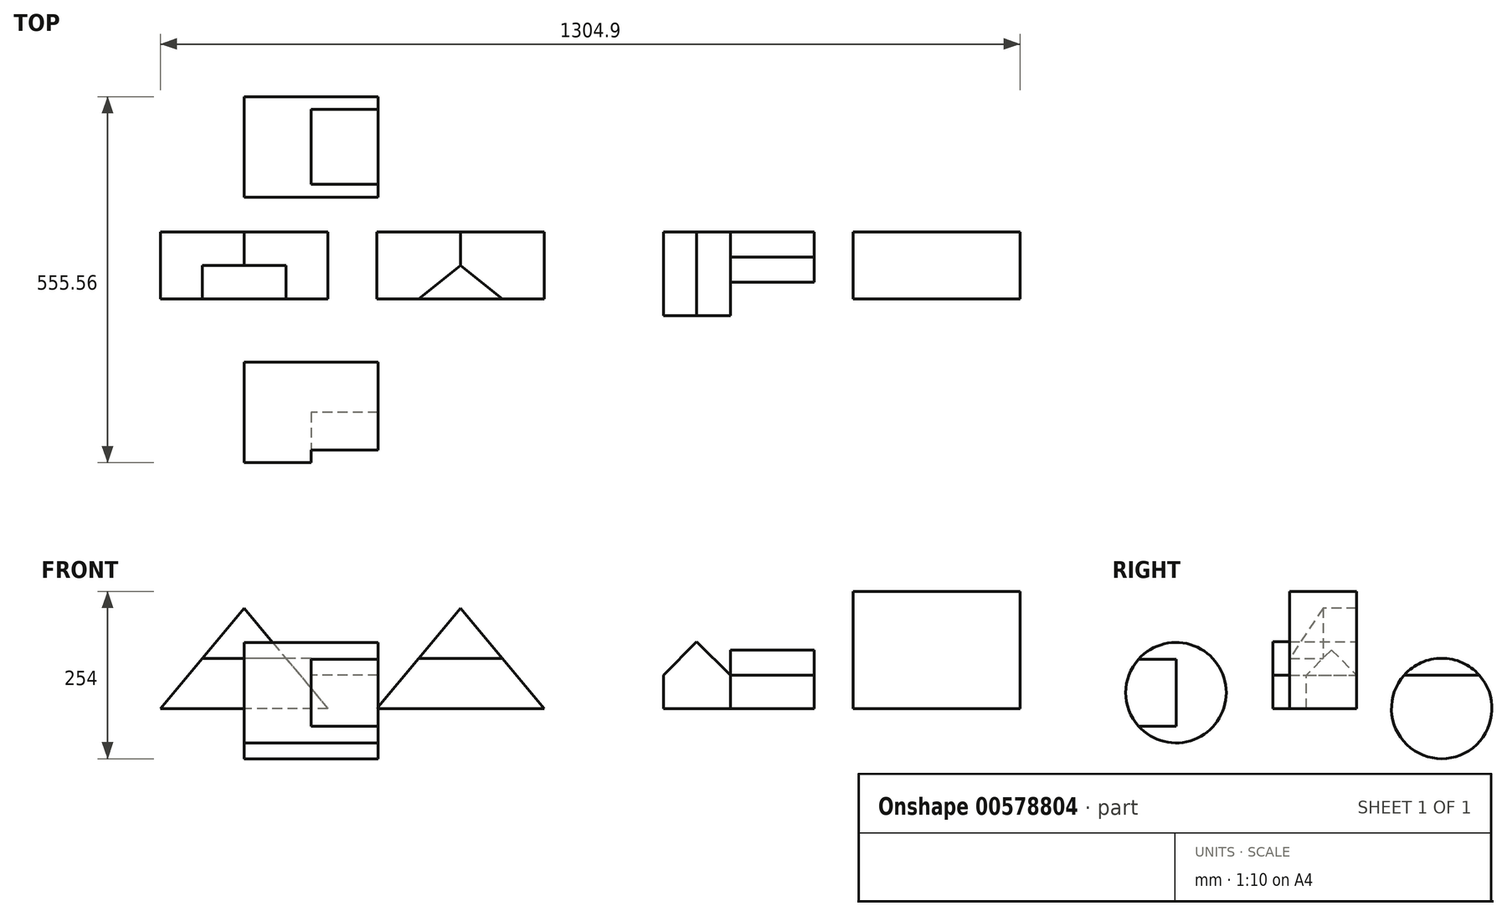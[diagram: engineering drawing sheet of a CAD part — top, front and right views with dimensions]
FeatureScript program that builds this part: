
annotation { "Feature Type Name" : "Feature", "Feature Type Description" : "" }
export const myFeature = defineFeature(function(context is Context, id is Id, definition is map)
    precondition{}
    {
        {
            var Q0;
            Q0=qCreatedBy(makeId("Front.planeOp"),FACE);
            var sketch = newSketch(context, id + "F0", { "sketchPlane" : qUnion([Q0])});
            skLineSegment(sketch, "E0", {"start": v(0, 0) * mm, "end": v(127, 0) * mm});
            skLineSegment(sketch, "E1", {"start": v(0, 0) * mm, "end": v(-127, 0) * mm});
            skLineSegment(sketch, "E2", {"start": v(0, 0) * mm, "end": v(0, 76.2) * mm});
            skLineSegment(sketch, "E3", {"start": v(0, 76.2) * mm, "end": v(0, 152.4) * mm});
            skLineSegment(sketch, "E4", {"start": v(0, 152.4) * mm, "end": v(127, 0) * mm});
            skLineSegment(sketch, "E5", {"start": v(0, 152.4) * mm, "end": v(-127, 0) * mm});
            skLineSegment(sketch, "E6", {"start": v(0, 76.2) * mm, "end": v(63.5, 76.2) * mm});
            skLineSegment(sketch, "E7", {"start": v(63.5, 76.2) * mm, "end": v(-63.5, 76.2) * mm});
            skSolve(sketch);
        }
        {
            var Q0;
            {var subQ0=sQuery(id+"F0.wireOp",EDGE,"E1");Q0=makeQuery(id+"F0.imprint","IMPRINT",FACE,{"disambiguationData":[TD([[makeQuery(id+"F0.imprint","IMPRINT",EDGE,{"derivedFrom":subQ0}),-1.0]])]});}
            var Q1;
            {var subQ0=sQuery(id+"F0.wireOp",EDGE,"E0");Q1=makeQuery(id+"F0.imprint","IMPRINT",FACE,{"disambiguationData":[TD([[makeQuery(id+"F0.imprint","IMPRINT",EDGE,{"derivedFrom":subQ0}),1.0]])]});}
            extrude(context, id + "F1", {"entities" : qUnion([Q0, Q1]), "depth" : 101.6 * mm, "offsetDistance" : 25.4 * mm});
        }
        {
            var Q0;
            Q0 = qSketchRegion(id + "F0", true);
            extrude(context, id + "F2", {"entities" : qUnion([Q0]), "operationType" : NewBodyOperationType.ADD, "depth" : 50.8 * mm, "offsetDistance" : 25.4 * mm});
        }
        {
            var Q0;
            Q0=qCreatedBy(makeId("Front.planeOp"),FACE);
            var sketch = newSketch(context, id + "F3", { "sketchPlane" : qUnion([Q0])});
            skLineSegment(sketch, "E8", {"start": v(201.55, 0) * mm, "end": v(455.55, 0) * mm});
            skLineSegment(sketch, "E9", {"start": v(201.55, 0) * mm, "end": v(201.55, 152.4) * mm});
            skLineSegment(sketch, "E10", {"start": v(201.55, 152.4) * mm, "end": v(455.55, 152.4) * mm});
            skLineSegment(sketch, "E11", {"start": v(455.55, 152.4) * mm, "end": v(455.55, 0) * mm});
            skSolve(sketch);
        }
        {
            var Q0;
            Q0=makeQuery(id+"F3.imprint","IMPRINT",FACE,{"disambiguationData":[TD([[makeQuery(id+"F3.imprint","IMPRINT",EDGE,{"derivedFrom":sQuery(id+"F3.wireOp",EDGE,"E8")}),1.0]])]});
            extrude(context, id + "F4", {"entities" : qUnion([Q0]), "depth" : 101.6 * mm, "offsetDistance" : 25.4 * mm});
        }
        {
            var Q0;
            Q0=makeQuery(id+"F4.opExtrude","SWEPT_FACE",FACE,{"disambiguationData":[OSD([sQuery(id+"F3.wireOp",EDGE,"E11")])]});
            var sketch = newSketch(context, id + "F5", { "sketchPlane" : qUnion([Q0])});
            skLineSegment(sketch, "E12", {"start": v(-50.8, 152.4) * mm, "end": v(-101.6, 76.2) * mm});
            skSolve(sketch);
        }
        {
            var Q0;
            Q0=makeQuery(id+"F4.opExtrude","CAP_FACE",FACE,{"disambiguationData":[OSD([sQuery(id+"F3.wireOp",EDGE,"E8"),sQuery(id+"F3.wireOp",EDGE,"E9"),sQuery(id+"F3.wireOp",EDGE,"E10"),sQuery(id+"F3.wireOp",EDGE,"E11")])],"isStart":false});
            var sketch = newSketch(context, id + "F6", { "sketchPlane" : qUnion([Q0])});
            skLineSegment(sketch, "E13", {"start": v(328.55, 152.4) * mm, "end": v(455.55, 0) * mm});
            skLineSegment(sketch, "E14", {"start": v(455.55, 0) * mm, "end": v(201.55, 0) * mm});
            skLineSegment(sketch, "E15", {"start": v(201.55, 0) * mm, "end": v(328.55, 152.4) * mm});
            skSolve(sketch);
        }
        {
            var Q0;
            {var subQ0=sQuery(id+"F5.wireOp",EDGE,"E12");Q0=makeQuery(id+"F5.imprint","IMPRINT",FACE,{"disambiguationData":[TD([[makeQuery(id+"F5.imprint","IMPRINT",EDGE,{"derivedFrom":subQ0}),-1.0]])]});}
            extrude(context, id + "F7", {"entities" : qUnion([Q0]), "operationType" : NewBodyOperationType.REMOVE, "oppositeDirection" : true, "depth" : 254 * mm, "offsetDistance" : 25.4 * mm});
        }
        {
            var Q0;
            {var subQ0=sQuery(id+"F6.wireOp",EDGE,"E15");Q0=makeQuery(id+"F6.imprint","IMPRINT",FACE,{"disambiguationData":[TD([[makeQuery(id+"F6.imprint","IMPRINT",EDGE,{"derivedFrom":subQ0}),1.0]])]});}
            extrude(context, id + "F8", {"entities" : qUnion([Q0]), "operationType" : NewBodyOperationType.REMOVE, "oppositeDirection" : true, "depth" : 101.6 * mm, "offsetDistance" : 25.4 * mm});
        }
        {
            var Q0;
            {var subQ0=sQuery(id+"F6.wireOp",EDGE,"E13");Q0=makeQuery(id+"F6.imprint","IMPRINT",FACE,{"disambiguationData":[TD([[makeQuery(id+"F6.imprint","IMPRINT",EDGE,{"derivedFrom":subQ0}),1.0]])]});}
            extrude(context, id + "F9", {"entities" : qUnion([Q0]), "operationType" : NewBodyOperationType.REMOVE, "oppositeDirection" : true, "depth" : 101.6 * mm, "offsetDistance" : 25.4 * mm});
        }
        {
            var Q0;
            Q0=qCreatedBy(makeId("Front.planeOp"),FACE);
            var sketch = newSketch(context, id + "F10", { "sketchPlane" : qUnion([Q0])});
            skLineSegment(sketch, "E16", {"start": v(636.4, 0) * mm, "end": v(738, 0) * mm});
            skLineSegment(sketch, "E17", {"start": v(738, 0) * mm, "end": v(738, 50.8) * mm});
            skLineSegment(sketch, "E18", {"start": v(686.75, 101.6) * mm, "end": v(738, 50.8) * mm});
            skLineSegment(sketch, "E19", {"start": v(636.4, 0) * mm, "end": v(636.4, 50.8) * mm});
            skLineSegment(sketch, "E20", {"start": v(636.4, 50.8) * mm, "end": v(686.75, 101.6) * mm});
            skSolve(sketch);
        }
        {
            var Q0;
            Q0=makeQuery(id+"F10.imprint","IMPRINT",FACE,{"disambiguationData":[TD([[makeQuery(id+"F10.imprint","IMPRINT",EDGE,{"derivedFrom":sQuery(id+"F10.wireOp",EDGE,"E16")}),1.0]])]});
            extrude(context, id + "F11", {"entities" : qUnion([Q0]), "depth" : 127 * mm, "offsetDistance" : 25.4 * mm});
        }
        {
            var Q0;
            Q0=makeQuery(id+"F11.opExtrude","SWEPT_FACE",FACE,{"disambiguationData":[OSD([sQuery(id+"F10.wireOp",EDGE,"E17")])]});
            cPlane(context, id + "F12", {"entities" : qUnion([Q0]), "cplaneType" : CPlaneType.OFFSET, "offset" : 127 * mm, "width" : 152.4 * mm, "height" : 152.4 * mm});
        }
        {
            var Q0;
            Q0=qCreatedBy(id+"F12.planeOp",FACE);
            var sketch = newSketch(context, id + "F13", { "sketchPlane" : qUnion([Q0])});
            skLineSegment(sketch, "E21", {"start": v(0, 0) * mm, "end": v(-76.2, 0) * mm});
            skLineSegment(sketch, "E22", {"start": v(-76.2, 0) * mm, "end": v(-76.2, 50.8) * mm});
            skLineSegment(sketch, "E23", {"start": v(0, 50.8) * mm, "end": v(0, 0) * mm});
            skLineSegment(sketch, "E24", {"start": v(-38.1, 88.9) * mm, "end": v(-76.2, 50.8) * mm});
            skLineSegment(sketch, "E25", {"start": v(-38.1, 88.9) * mm, "end": v(0, 50.8) * mm});
            skSolve(sketch);
        }
        {
            var Q0;
            Q0=makeQuery(id+"F13.imprint","IMPRINT",FACE,{"disambiguationData":[TD([[makeQuery(id+"F13.imprint","IMPRINT",EDGE,{"derivedFrom":sQuery(id+"F13.wireOp",EDGE,"E21")}),-1.0]])]});
            extrude(context, id + "F14", {"entities" : qUnion([Q0]), "operationType" : NewBodyOperationType.ADD, "oppositeDirection" : true, "depth" : 127 * mm, "offsetDistance" : 25.4 * mm});
        }
        {
            var Q0;
            Q0=qCreatedBy(makeId("Right.planeOp"),FACE);
            var sketch = newSketch(context, id + "F15", { "sketchPlane" : qUnion([Q0])});
            skCircle(sketch, "E26", {"center": v(129.16, 0) * mm, "radius": 76.2 * mm});
            skLineSegment(sketch, "E27", {"start": v(129.16, 50.8) * mm, "end": v(185.95, 50.8) * mm});
            skLineSegment(sketch, "E28", {"start": v(129.16, 50.8) * mm, "end": v(72.36, 50.8) * mm});
            skSolve(sketch);
        }
        {
            var Q0;
            {var subQ0=sQuery(id+"F15.wireOp",EDGE,"E27");Q0=makeQuery(id+"F15.imprint","IMPRINT",FACE,{"disambiguationData":[TD([[makeQuery(id+"F15.imprint","IMPRINT",EDGE,{"derivedFrom":subQ0}),-1.0]])]});}
            extrude(context, id + "F16", {"entities" : qUnion([Q0]), "depth" : 203.2 * mm, "offsetDistance" : 25.4 * mm});
        }
        {
            var Q0;
            Q0 = qSketchRegion(id + "F15", true);
            extrude(context, id + "F17", {"entities" : qUnion([Q0]), "operationType" : NewBodyOperationType.ADD, "depth" : 101.6 * mm, "offsetDistance" : 25.4 * mm});
        }
        {
            var Q0;
            Q0=qCreatedBy(makeId("Right.planeOp"),FACE);
            var sketch = newSketch(context, id + "F18", { "sketchPlane" : qUnion([Q0])});
            skCircle(sketch, "E29", {"center": v(-274, 23.97) * mm, "radius": 76.2 * mm});
            skLineSegment(sketch, "E30", {"start": v(-274, 23.97) * mm, "end": v(-274, 74.77) * mm});
            skLineSegment(sketch, "E31", {"start": v(-274, 23.97) * mm, "end": v(-274, -26.83) * mm});
            skLineSegment(sketch, "E32", {"start": v(-274, 74.77) * mm, "end": v(-330.8, 74.77) * mm});
            skLineSegment(sketch, "E33", {"start": v(-274, -26.83) * mm, "end": v(-330.8, -26.83) * mm});
            skSolve(sketch);
        }
        {
            var Q0;
            Q0=makeQuery(id+"F18.imprint","IMPRINT",FACE,{"disambiguationData":[TD([[makeQuery(id+"F18.imprint","IMPRINT",EDGE,{"derivedFrom":sQuery(id+"F18.wireOp",EDGE,"E30")}),-1.0]])]});
            extrude(context, id + "F19", {"entities" : qUnion([Q0]), "depth" : 203.2 * mm, "offsetDistance" : 25.4 * mm});
        }
        {
            var Q0;
            Q0 = qSketchRegion(id + "F18", true);
            extrude(context, id + "F20", {"entities" : qUnion([Q0]), "operationType" : NewBodyOperationType.ADD, "depth" : 101.6 * mm, "offsetDistance" : 25.4 * mm});
        }
        {
            var Q0;
            Q0=qCreatedBy(makeId("Front.planeOp"),FACE);
            var sketch = newSketch(context, id + "F21", { "sketchPlane" : qUnion([Q0])});
            skLineSegment(sketch, "E34", {"start": v(923.9, 0) * mm, "end": v(1177.9, 0) * mm});
            skLineSegment(sketch, "E35", {"start": v(1177.9, 0) * mm, "end": v(1177.9, 177.8) * mm});
            skLineSegment(sketch, "E36", {"start": v(923.9, 0) * mm, "end": v(923.9, 177.8) * mm});
            skLineSegment(sketch, "E37", {"start": v(923.9, 177.8) * mm, "end": v(1177.9, 177.8) * mm});
            skLineSegment(sketch, "E38", {"start": v(923.9, 88.9) * mm, "end": v(1177.9, 88.9) * mm});
            skSolve(sketch);
        }
        {
            var Q0;
            {var subQ0=sQuery(id+"F21.wireOp",EDGE,"E34");Q0=makeQuery(id+"F21.imprint","IMPRINT",FACE,{"disambiguationData":[TD([[makeQuery(id+"F21.imprint","IMPRINT",EDGE,{"derivedFrom":subQ0}),1.0]])]});}
            var Q1;
            {var subQ0=sQuery(id+"F21.wireOp",EDGE,"E37");Q1=makeQuery(id+"F21.imprint","IMPRINT",FACE,{"disambiguationData":[TD([[makeQuery(id+"F21.imprint","IMPRINT",EDGE,{"derivedFrom":subQ0}),-1.0]])]});}
            extrude(context, id + "F22", {"entities" : qUnion([Q0, Q1]), "depth" : 101.6 * mm, "offsetDistance" : 25.4 * mm});
        }
        {
            var Q0;
            Q0=makeQuery(id+"F22.opExtrude","CAP_FACE",FACE,{"disambiguationData":[OSD([sQuery(id+"F21.wireOp",EDGE,"E34"),sQuery(id+"F21.wireOp",EDGE,"E35"),sQuery(id+"F21.wireOp",EDGE,"E36"),sQuery(id+"F21.wireOp",EDGE,"E37")])],"isStart":false});
            var sketch = newSketch(context, id + "F23", { "sketchPlane" : qUnion([Q0])});
            skCircle(sketch, "E39", {"center": v(1050.9, 177.8) * mm, "radius": 76.2 * mm});
            skSolve(sketch);
        }
        {
            var Q0;
            {var subQ0=sQuery(id+"F23.wireOp",EDGE,"E39");var subQ1=makeQuery(id+"F22.opExtrude","CAP_EDGE",EDGE,{"disambiguationData":[OSD([sQuery(id+"F21.wireOp",EDGE,"E37")])],"isStart":false});var subQ2=makeQuery(id+"F23.imprint","INTERSECT",VERTEX,{"disambiguationData":[OD(0.0)],"derivedFrom":[subQ1,subQ0]});Q0=makeQuery(id+"F23.imprint","IMPRINT",FACE,{"disambiguationData":[TD([[makeQuery(id+"F23.imprint","IMPRINT",EDGE,{"disambiguationData":[TD([[subQ2,1.0]])],"derivedFrom":subQ0}),1.0]])]});}
            extrude(context, id + "F24", {"entities" : qUnion([Q0]), "operationType" : NewBodyOperationType.REMOVE, "oppositeDirection" : true, "depth" : 101.6 * mm, "offsetDistance" : 25.4 * mm});
        }
    });
